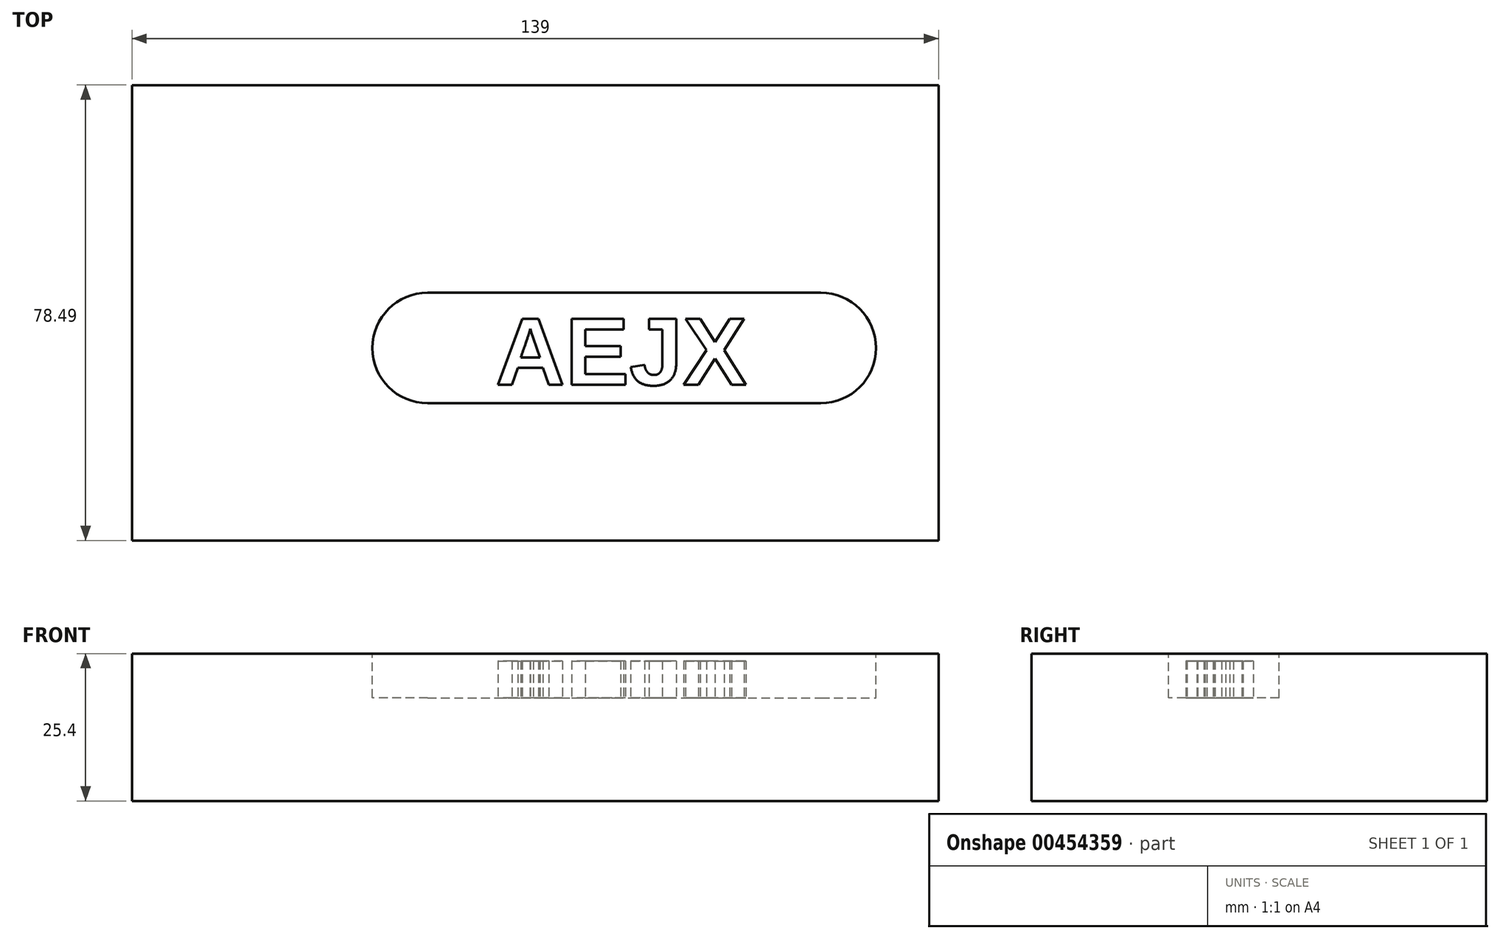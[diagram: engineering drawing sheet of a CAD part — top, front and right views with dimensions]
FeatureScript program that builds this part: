
annotation { "Feature Type Name" : "Feature", "Feature Type Description" : "" }
export const myFeature = defineFeature(function(context is Context, id is Id, definition is map)
    precondition{}
    {
        {
            var Q0;
            Q0=qCreatedBy(makeId("Top.planeOp"),FACE);
            var sketch = newSketch(context, id + "F0", { "sketchPlane" : qUnion([Q0])});
            skLineSegment(sketch, "E0.bottom", {"start": v(0, 0) * mm, "end": v(139, 0) * mm});
            skLineSegment(sketch, "E0.top", {"start": v(0, 78.49) * mm, "end": v(139, 78.49) * mm});
            skLineSegment(sketch, "E0.left", {"start": v(0, 0) * mm, "end": v(0, 78.49) * mm});
            skLineSegment(sketch, "E0.right", {"start": v(139, 0) * mm, "end": v(139, 78.49) * mm});
            skSolve(sketch);
        }
        {
            var Q0;
            Q0 = qSketchRegion(id + "F0", true);
            extrude(context, id + "F1", {"entities" : qUnion([Q0]), "depth" : 25.4 * mm});
        }
        {
            var Q0;
            Q0=makeQuery(id+"F1.opExtrude","CAP_FACE",FACE,{"disambiguationData":[OSD([sQuery(id+"F0.wireOp",EDGE,"E0.bottom"),sQuery(id+"F0.wireOp",EDGE,"E0.top"),sQuery(id+"F0.wireOp",EDGE,"E0.left"),sQuery(id+"F0.wireOp",EDGE,"E0.right")])],"isStart":false});
            var sketch = newSketch(context, id + "F2", { "sketchPlane" : qUnion([Q0])});
            skLineSegment(sketch, "E1.bottom", {"start": v(50.96, 42.69) * mm, "end": v(118.7, 42.69) * mm});
            skLineSegment(sketch, "E1.top", {"start": v(50.96, 23.64) * mm, "end": v(118.7, 23.64) * mm});
            skArc(sketch, "E2", {"start": v(50.96, 42.69) * mm, "mid": v(41.44, 33.16) * mm, "end": v(50.96, 23.64) * mm});
            skArc(sketch, "E3", {"start": v(118.7, 23.64) * mm, "mid": v(128.22, 33.16) * mm, "end": v(118.7, 42.69) * mm});
            skSolve(sketch);
        }
        {
            var Q0;
            Q0=makeQuery(id+"F2.imprint","IMPRINT",FACE,{"disambiguationData":[TD([[makeQuery(id+"F2.imprint","IMPRINT",EDGE,{"derivedFrom":sQuery(id+"F2.wireOp",EDGE,"E1.bottom")}),-1.0]])]});
            extrude(context, id + "F3", {"entities" : qUnion([Q0]), "operationType" : NewBodyOperationType.REMOVE, "oppositeDirection" : true, "depth" : 7.62 * mm});
        }
        {
            var Q0;
            Q0=makeQuery(id+"F3.boolean.opBoolean","COPY",FACE,{"derivedFrom":makeQuery(id+"F3.opExtrude","CAP_FACE",FACE,{"disambiguationData":[OSD([sQuery(id+"F2.wireOp",EDGE,"E1.bottom"),sQuery(id+"F2.wireOp",EDGE,"E1.top"),sQuery(id+"F2.wireOp",EDGE,"E2"),sQuery(id+"F2.wireOp",EDGE,"E3")])],"isStart":false})});
            var sketch = newSketch(context, id + "F4", { "sketchPlane" : qUnion([Q0])});
            skText(sketch, "E4", { "text": "AEJX", "fontName": "Arimo-Bold.ttf"});
            const initialGuessF4  = {"E4": [0.06266, 0.02681, 1, 0, 0.01194]};
            skSetInitialGuess(sketch, initialGuessF4);
            skSolve(sketch);
        }
        {
            var Q0;
            Q0 = qSketchRegion(id + "F4", true);
            extrude(context, id + "F5", {"entities" : qUnion([Q0]), "operationType" : NewBodyOperationType.ADD, "depth" : 6.35 * mm});
        }
    });
